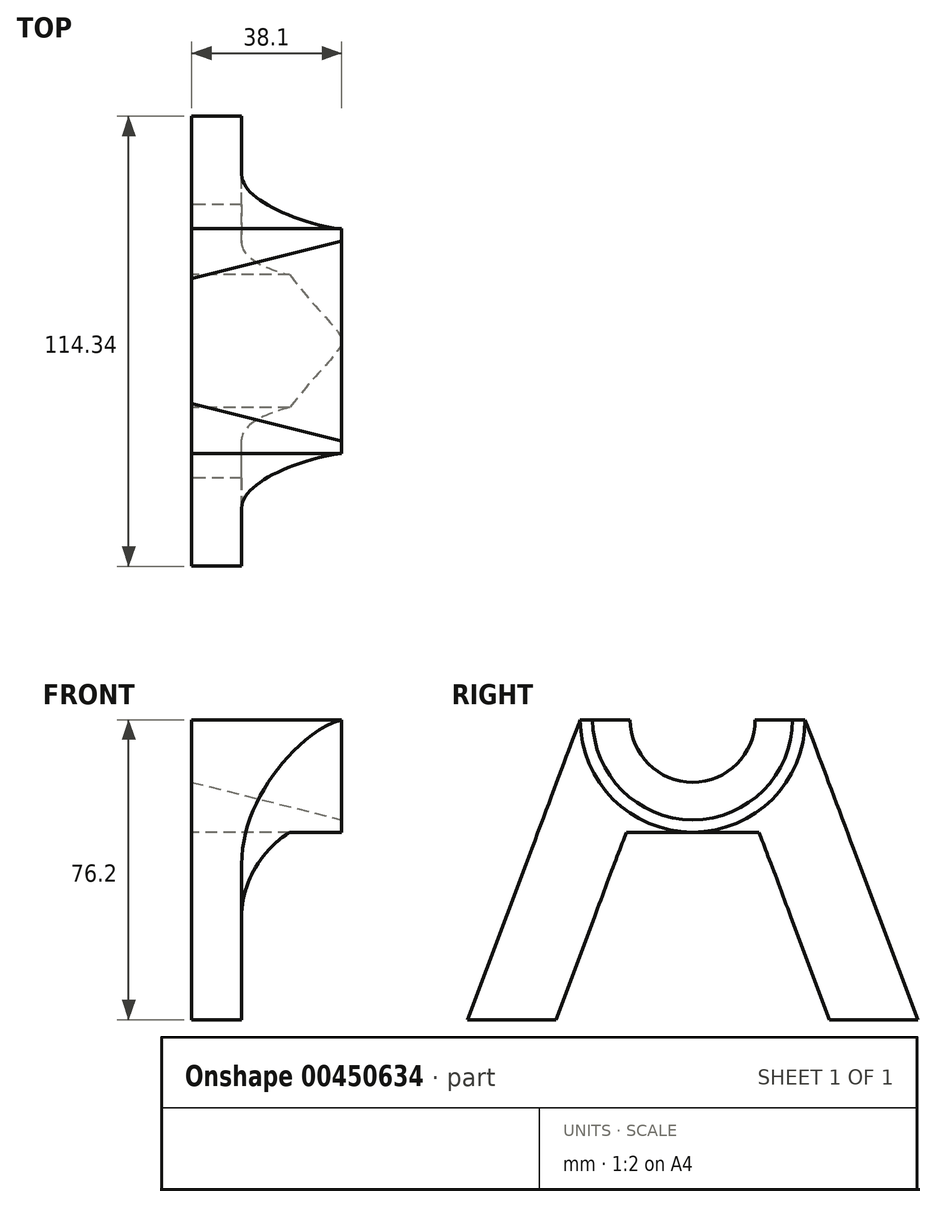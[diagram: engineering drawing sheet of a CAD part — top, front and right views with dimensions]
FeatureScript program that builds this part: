
annotation { "Feature Type Name" : "Feature", "Feature Type Description" : "" }
export const myFeature = defineFeature(function(context is Context, id is Id, definition is map)
    precondition{}
    {
        {
            var Q0;
            Q0=qCreatedBy(makeId("Right.planeOp"),FACE);
            var sketch = newSketch(context, id + "F0", { "sketchPlane" : qUnion([Q0])});
            skLineSegment(sketch, "E0", {"start": v(-34.75, 0) * mm, "end": v(-57.17, 0) * mm});
            skLineSegment(sketch, "E1", {"start": v(-57.17, 0) * mm, "end": v(-28.57, 76.2) * mm});
            skLineSegment(sketch, "E2", {"start": v(-28.58, 76.2) * mm, "end": v(-15.87, 76.2) * mm});
            skLineSegment(sketch, "E3", {"start": v(-34.75, 0) * mm, "end": v(-16.88, 47.62) * mm});
            skLineSegment(sketch, "E4", {"start": v(-16.88, 47.62) * mm, "end": v(0, 47.62) * mm});
            skArc(sketch, "E5", {"start": v(-15.87, 76.2) * mm, "mid": v(-11.23, 64.97) * mm, "end": v(0, 60.33) * mm});
            skLineSegment(sketch, "E6", {"start": v(0, 60.33) * mm, "end": v(0, 47.62) * mm});
            skSolve(sketch);
        }
        {
            var Q0;
            Q0 = qSketchRegion(id + "F0", true);
            extrude(context, id + "F1", {"entities" : qUnion([Q0]), "depth" : 12.7 * mm});
        }
        {
            var Q0;
            Q0=makeQuery(id+"F1.opExtrude","SWEPT_BODY",BODY,{"disambiguationData":[OSD([sQuery(id+"F0.wireOp",EDGE,"E0"),sQuery(id+"F0.wireOp",EDGE,"E1"),sQuery(id+"F0.wireOp",EDGE,"E2"),sQuery(id+"F0.wireOp",EDGE,"E3"),sQuery(id+"F0.wireOp",EDGE,"E4"),sQuery(id+"F0.wireOp",EDGE,"E5"),sQuery(id+"F0.wireOp",EDGE,"E6")])]});
            var Q1;
            Q1=qCreatedBy(makeId("Front.planeOp"),FACE);
            mirror(context, id + "F2", {"operationType" : NewBodyOperationType.ADD, "entities" : qUnion([Q0]), "mirrorPlane" : qUnion([Q1])});
        }
        {
            var Q0;
            Q0=makeQuery(id+"F1.opExtrude","SWEPT_FACE",FACE,{"disambiguationData":[OSD([sQuery(id+"F0.wireOp",EDGE,"E2")])]});
            var sketch = newSketch(context, id + "F3", { "sketchPlane" : qUnion([Q0])});
            skLineSegment(sketch, "E7", {"start": v(0, -15.88) * mm, "end": v(12.7, -19.05) * mm});
            skLineSegment(sketch, "E8", {"start": v(12.7, -19.05) * mm, "end": v(12.7, -15.87) * mm});
            skLineSegment(sketch, "E9", {"start": v(12.7, -15.87) * mm, "end": v(0, -15.87) * mm});
            skLineSegment(sketch, "E10", {"start": v(20.77, 0) * mm, "end": v(-9.65, 0) * mm, "construction": true});
            skSolve(sketch);
        }
        {
            var Q0;
            Q0 = qSketchRegion(id + "F3", true);
            var Q1;
            Q1=sQuery(id+"F3.wireOp",EDGE,"E10");
            revolve(context, id + "F4", {"operationType" : NewBodyOperationType.REMOVE, "entities" : qUnion([Q0]), "axis" : qUnion([Q1]), "revolveType" : RevolveType.FULL, "oppositeDirection" : true});
        }
        {
            var Q0;
            Q0=makeQuery(id+"F1.opExtrude","SWEPT_FACE",FACE,{"disambiguationData":[OSD([sQuery(id+"F0.wireOp",EDGE,"E2")])]});
            var sketch = newSketch(context, id + "F5", { "sketchPlane" : qUnion([Q0])});
            skLineSegment(sketch, "E11", {"start": v(12.7, -19.05) * mm, "end": v(38.1, -25.4) * mm});
            skLineSegment(sketch, "E12", {"start": v(38.1, -25.4) * mm, "end": v(38.1, -28.57) * mm});
            skLineSegment(sketch, "E13", {"start": v(38.1, -28.57) * mm, "end": v(12.7, -28.57) * mm});
            skLineSegment(sketch, "E14", {"start": v(12.7, -28.57) * mm, "end": v(12.7, -19.05) * mm});
            skLineSegment(sketch, "E15", {"start": v(0, 0) * mm, "end": v(38.9, 0) * mm, "construction": true});
            skSolve(sketch);
        }
        {
            var Q0;
            Q0 = qSketchRegion(id + "F5", true);
            var Q1;
            Q1=sQuery(id+"F5.wireOp",EDGE,"E15");
            revolve(context, id + "F6", {"operationType" : NewBodyOperationType.ADD, "entities" : qUnion([Q0]), "axis" : qUnion([Q1]), "revolveType" : RevolveType.ONE_DIRECTION, "angle" : 180 * degree});
        }
        {
            var Q0;
            {var subQ2=sQuery(id+"F0.wireOp",EDGE,"E2");var subQ3=sQuery(id+"F0.wireOp",EDGE,"E1");var subQ5=sQuery(id+"F5.wireOp",EDGE,"E14");var subQ6=sQuery(id+"F5.wireOp",EDGE,"E13");Q0=makeQuery(id+"F6.boolean.opBoolean","SPLIT",EDGE,{"disambiguationData":[TD([makeQuery(id+"F1.opExtrude","SWEPT_FACE",FACE,{"disambiguationData":[OSD([subQ3])]})])],"derivedFrom":makeQuery(id+"F6.opRevolve","SWEPT_EDGE",EDGE,{"disambiguationData":[OSD([subQ3,subQ2,subQ6,subQ5])]})});}
            fillet(context, id + "F7", {"entities" : qUnion([Q0]), "radius" : 27.6 * mm, "tangentPropagation" : true, "allowEdgeOverflow" : false});
        }
    });
